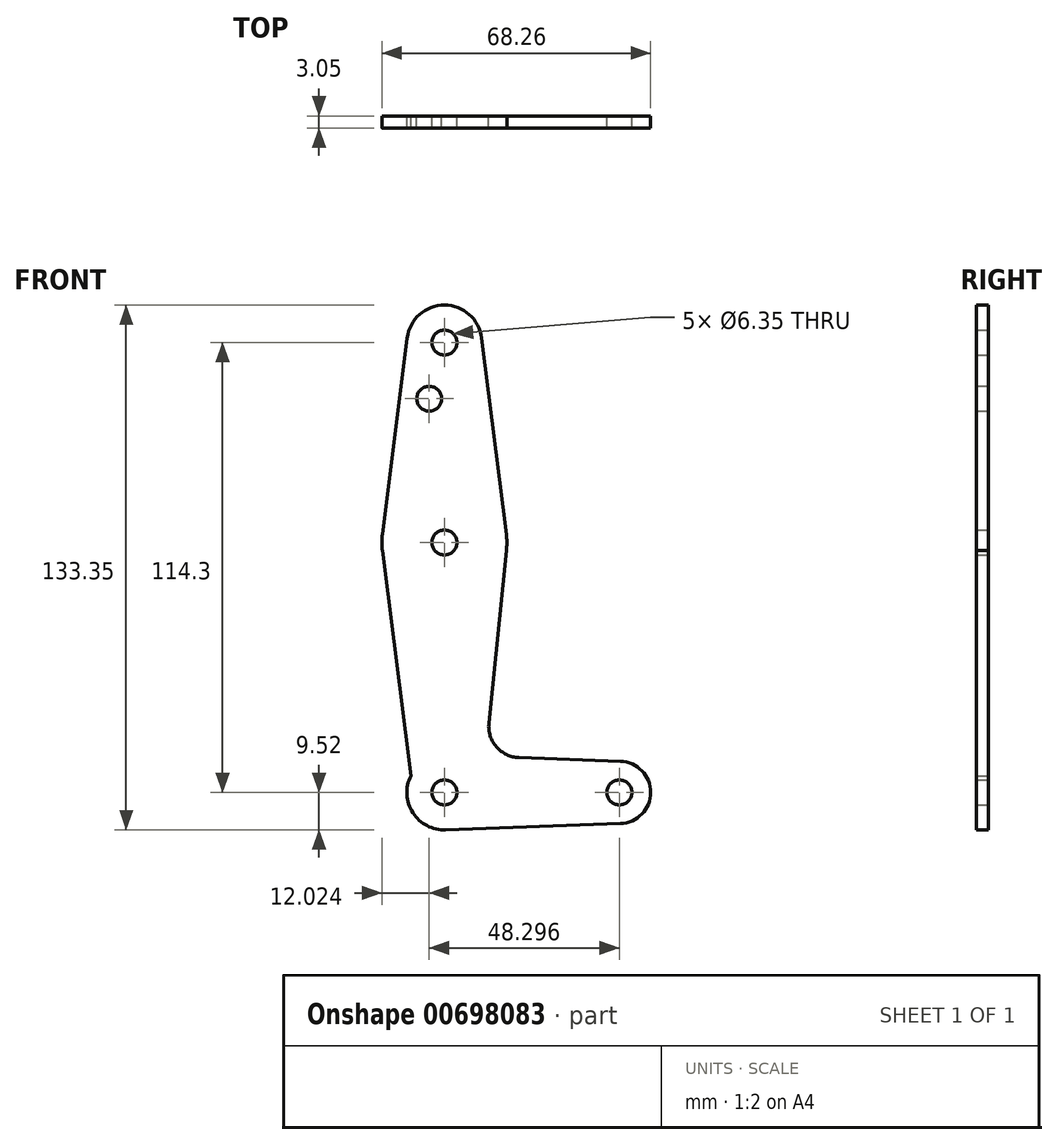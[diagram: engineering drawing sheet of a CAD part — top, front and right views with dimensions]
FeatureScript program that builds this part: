
annotation { "Feature Type Name" : "Feature", "Feature Type Description" : "" }
export const myFeature = defineFeature(function(context is Context, id is Id, definition is map)
    precondition{}
    {
        {
            var Q0;
            Q0=qCreatedBy(makeId("Front.planeOp"),FACE);
            var sketch = newSketch(context, id + "F0", { "sketchPlane" : qUnion([Q0])});
            skLineSegment(sketch, "E0", {"start": v(0, 0) * mm, "end": v(0, 114.3) * mm, "construction": true});
            skLineSegment(sketch, "E1", {"start": v(0, 0) * mm, "end": v(44.45, 0) * mm, "construction": true});
            skCircle(sketch, "E2", {"center": v(0, 0) * mm, "radius": 9.53 * mm});
            skCircle(sketch, "E3", {"center": v(44.45, 0) * mm, "radius": 7.94 * mm});
            skCircle(sketch, "E4", {"center": v(0, 114.3) * mm, "radius": 9.53 * mm});
            skCircle(sketch, "E5", {"center": v(0, 63.5) * mm, "radius": 15.88 * mm});
            skLineSegment(sketch, "E6", {"start": v(-9.45, 115.5) * mm, "end": v(-15.75, 65.48) * mm});
            skLineSegment(sketch, "E7", {"start": v(15.75, 65.48) * mm, "end": v(9.45, 115.5) * mm});
            skLineSegment(sketch, "E8", {"start": v(-15.75, 61.52) * mm, "end": v(-8, 0) * mm});
            skLineSegment(sketch, "E9", {"start": v(11.3, 17.6) * mm, "end": v(15.75, 61.52) * mm});
            skLineSegment(sketch, "E10", {"start": v(18.93, 8.85) * mm, "end": v(44.73, 7.93) * mm});
            skLineSegment(sketch, "E11", {"start": v(44.73, -7.93) * mm, "end": v(0, -9.53) * mm});
            skCircle(sketch, "E12", {"center": v(0, 114.3) * mm, "radius": 3.18 * mm});
            skCircle(sketch, "E13", {"center": v(0, 63.5) * mm, "radius": 3.18 * mm});
            skCircle(sketch, "E14", {"center": v(0, 0) * mm, "radius": 3.18 * mm});
            skCircle(sketch, "E15", {"center": v(44.45, 0) * mm, "radius": 3.18 * mm});
            skCircle(sketch, "E16", {"center": v(-3.85, 100.03) * mm, "radius": 3.18 * mm});
            skPoint(sketch, "E17.newPointA", {"position": v(9.52, 0) * mm});
            skArc(sketch, "E17.filletArc", {"start": v(11.3, 17.6) * mm, "mid": v(13.22, 11.57) * mm, "end": v(18.93, 8.85) * mm});
            skSolve(sketch);
        }
        {
            var Q0;
            Q0 = qSketchRegion(id + "F0", true);
            extrude(context, id + "F1", {"entities" : qUnion([Q0]), "depth" : 3.05 * mm, "offsetDistance" : 25.4 * mm});
        }
    });
